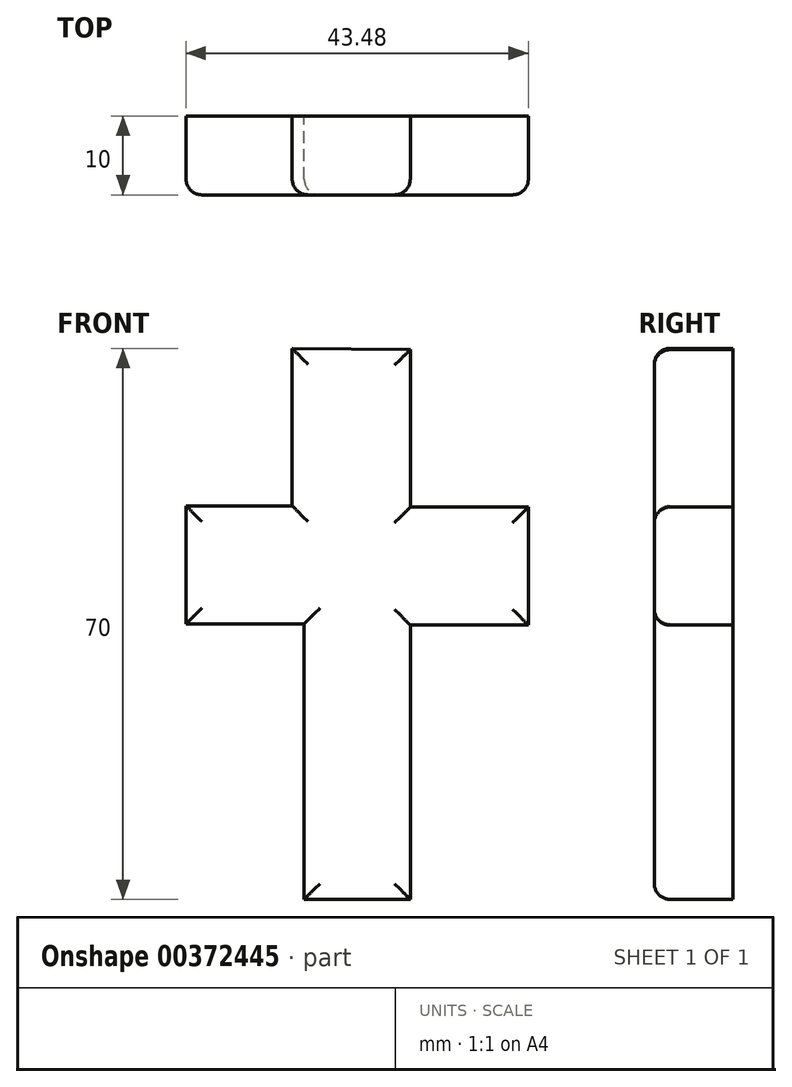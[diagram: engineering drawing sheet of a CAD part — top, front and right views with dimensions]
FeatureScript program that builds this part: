
annotation { "Feature Type Name" : "Feature", "Feature Type Description" : "" }
export const myFeature = defineFeature(function(context is Context, id is Id, definition is map)
    precondition{}
    {
        {
            var Q0;
            Q0=qCreatedBy(makeId("Front.planeOp"),FACE);
            var sketch = newSketch(context, id + "F0", { "sketchPlane" : qUnion([Q0])});
            skLineSegment(sketch, "E0", {"start": v(-15, 26.32) * mm, "end": v(-15, 6.32) * mm});
            skLineSegment(sketch, "E1", {"start": v(-15, 6.32) * mm, "end": v(-28.48, 6.32) * mm});
            skLineSegment(sketch, "E2", {"start": v(-28.48, 6.32) * mm, "end": v(-28.48, -8.68) * mm});
            skLineSegment(sketch, "E3", {"start": v(-28.48, -8.68) * mm, "end": v(-13.48, -8.68) * mm});
            skLineSegment(sketch, "E4", {"start": v(-13.48, -8.68) * mm, "end": v(-13.48, -43.68) * mm});
            skLineSegment(sketch, "E5", {"start": v(-13.48, -43.68) * mm, "end": v(0, -43.68) * mm});
            skLineSegment(sketch, "E6", {"start": v(0, -43.68) * mm, "end": v(0, -8.84) * mm});
            skLineSegment(sketch, "E7", {"start": v(0, -8.84) * mm, "end": v(15, -8.84) * mm});
            skLineSegment(sketch, "E8", {"start": v(15, -8.84) * mm, "end": v(15, 6.16) * mm});
            skLineSegment(sketch, "E9", {"start": v(15, 6.16) * mm, "end": v(0, 6.16) * mm});
            skLineSegment(sketch, "E10", {"start": v(0, 6.16) * mm, "end": v(0, 26.16) * mm});
            skLineSegment(sketch, "E11", {"start": v(0, 26.16) * mm, "end": v(-15, 26.32) * mm});
            skSolve(sketch);
        }
        {
            var Q0;
            Q0=qSketchRegion(id+"F0",true);
            extrude(context, id + "F1", {"entities" : qUnion([Q0]), "depth" : 10 * mm});
        }
        {
            var Q0;
            Q0=makeQuery(id+"F1.opExtrude","CAP_FACE",FACE,{"disambiguationData":[OSD([sQuery(id+"F0.wireOp",EDGE,"E0"),sQuery(id+"F0.wireOp",EDGE,"E1"),sQuery(id+"F0.wireOp",EDGE,"E2"),sQuery(id+"F0.wireOp",EDGE,"E3"),sQuery(id+"F0.wireOp",EDGE,"E4"),sQuery(id+"F0.wireOp",EDGE,"E5"),sQuery(id+"F0.wireOp",EDGE,"E6"),sQuery(id+"F0.wireOp",EDGE,"E7"),sQuery(id+"F0.wireOp",EDGE,"E8"),sQuery(id+"F0.wireOp",EDGE,"E9"),sQuery(id+"F0.wireOp",EDGE,"E10"),sQuery(id+"F0.wireOp",EDGE,"E11")])],"isStart":false});
            fillet(context, id + "F2", {"entities" : qUnion([Q0]), "radius" : 2 * mm, "tangentPropagation" : true, "allowEdgeOverflow" : false});
        }
    });
